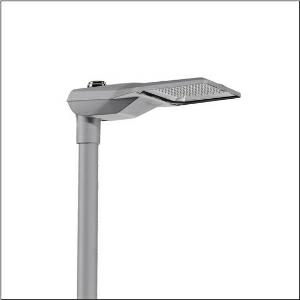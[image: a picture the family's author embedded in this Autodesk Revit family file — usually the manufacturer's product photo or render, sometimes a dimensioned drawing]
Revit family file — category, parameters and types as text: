
# Revit family: streetlight_sl_21_midi___st0_5a_5xe7b47n08nb_57a0
name_source: partatom
category: Lighting Fixtures
units: mm (PartAtom-declared; Revit-internal decimal feet)

## family parameters
Cut with Voids When Loaded = No
Host = Face
Light Source = No
Part Type = Normal
Room Calculation Point = No
Round Connector Dimension = Use Diameter
Shared = No

## types (1)
- --- (1 x LED, 23710 lm, 151.2 W, 4000K)
    Apparent Load = 151 VA
    CIE Flux Codes = 43 76 97 100 100
    Color Rendering = 70
    Color Temperature = 4000K
    Default Elevation = 1800 mm
    Description = Streetlight SL 21 midi, mast luminaire, primary light control with lens, of PMMA, primary optical cover: cover, of toughened safety glass, transparent, light distribution: ST0.5a, light emission: direct distribution, primary light characteristic: asymmetric, installation type: side-entry, LED, 3G 2.5mm², High Power LED, rated luminous flux: 23.710lm, luminous efficacy: 157lm/W, light colour: 740, colour temperature: 4000K, control gear: NEMA (7pin), control: overheat protection, pre-setting: linear dimming characteristic, constant luminous flux control, time-dependent luminous flux control, flexible luminous flux parameterisation, mains connection: 220..240V, AC, 50/60Hz, connection cable pre-assembled, cable length: 12,5m, wiring characteristics: H05VV-F, start of lifetime: 151W, end of service life: 157W, reduction: 70W, luminaire housing, of diecast aluminium (EN AC-44300), powder-coated, Siteco® metallic grey (DB 702S), corrosivity category C5 mid according to DIN EN ISO 12944, multi-level sealing system, sealing non-destructively replaceable, inclination adjustable: 0°, 5°, 10°, 15°, length: 644mm, width: 335mm, height: 110mm, spigot size: 42mm (side-entry), mounting height: 4..8m, protection rating (complete): IP66, insulation class (complete): insulation class I (protective earthing), certification: CE, ENEC, ENEC+, VDE, impact resistance: IK10, permissible operating ambient temperature for outdoor applications: -40..+50°C, standard-compliant lighting for roads and squares, packaging unit: 1 piece

Light Distribution: ST0.5a
    Height = 111 mm
    Lamp = 1 x LED
    Lamp Light Flux = 23710 lm
    Lamp Power = 151.2 W
    Lamp count = 1
    Length = 644 mm
    Luminous efficacy = 157 lm/W
    Manufacturer = Siteco
    ModVariant = No
    Model = 5XE7B47N08NB
    Number of Poles = 1
    OnlyDefault = Yes
    Power Factor = 1
    Product Name = Streetlight SL 21 midi | ST0.5a
    Product group = mast luminaire | pylon top
    ProductGroupID = 6100
    Protection Class = Protection class I
    Protection Degree = IP 66
    RLX_Detail_Level = 1
    RLX_Emergency_Light_Flux = 0 lm
    RLX_Emergency_Type = 0
    RLX_Emergency_Type_DB = No
    RlxData = <blob elided: 37829 chars, md5=1efdbe79>
    Socket = socket
    Standby Power = 0 W
    System Light Flux = 23710 lm
    System Power = 151 W
    Type Comments = factory setting: luminous flux: 100 % | dim-lin: 254 | 802 mA
    Type Image = l_1294377.jpg
    URL = http://relux.com
    VarID = @adj_136654
    Voltage = 0 V
    Weight = 0.00 kg
    Width = 336 mm

## geometry (parser evidence)
native form markers: Blend x4, Sweep x9
no freeform markers — native parametric forms only
